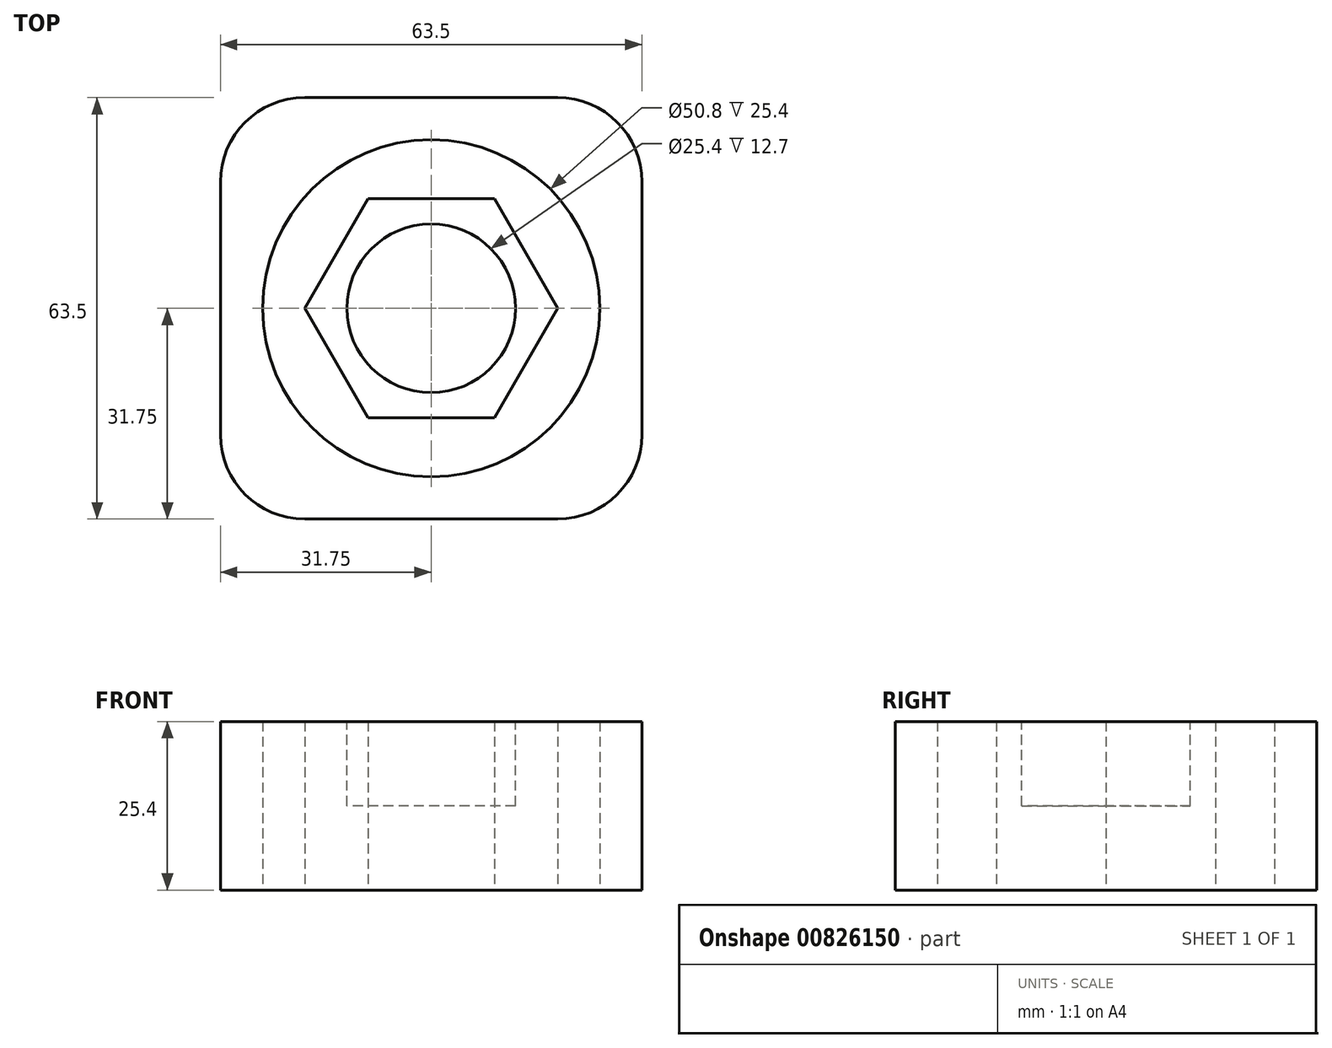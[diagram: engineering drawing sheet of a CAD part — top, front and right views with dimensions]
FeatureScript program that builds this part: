
annotation { "Feature Type Name" : "Feature", "Feature Type Description" : "" }
export const myFeature = defineFeature(function(context is Context, id is Id, definition is map)
    precondition{}
    {
        {
            var Q0;
            Q0=qCreatedBy(makeId("Top.planeOp"),FACE);
            var sketch = newSketch(context, id + "F0", { "sketchPlane" : qUnion([Q0])});
            skCircle(sketch, "E0", {"center": v(0, 0) * mm, "radius": 25.4 * mm});
            skLineSegment(sketch, "E1.bottom", {"start": v(19.05, 31.75) * mm, "end": v(-19.05, 31.75) * mm});
            skLineSegment(sketch, "E1.top", {"start": v(19.05, -31.75) * mm, "end": v(-19.05, -31.75) * mm});
            skLineSegment(sketch, "E1.left", {"start": v(31.75, 19.05) * mm, "end": v(31.75, -19.05) * mm});
            skLineSegment(sketch, "E1.right", {"start": v(-31.75, 19.05) * mm, "end": v(-31.75, -19.05) * mm});
            skCircle(sketch, "E2.cCircle", {"center": v(0, 0) * mm, "radius": 19.05 * mm, "construction": true});
            skLineSegment(sketch, "E2.0", {"start": v(9.53, -16.5) * mm, "end": v(-9.52, -16.5) * mm});
            skLineSegment(sketch, "E2.1", {"start": v(-9.52, -16.5) * mm, "end": v(-19.05, 0) * mm});
            skLineSegment(sketch, "E2.2", {"start": v(-19.05, 0) * mm, "end": v(-9.53, 16.5) * mm});
            skLineSegment(sketch, "E2.3", {"start": v(-9.53, 16.5) * mm, "end": v(9.52, 16.5) * mm});
            skLineSegment(sketch, "E2.4", {"start": v(9.52, 16.5) * mm, "end": v(19.05, 0) * mm});
            skLineSegment(sketch, "E2.5", {"start": v(19.05, 0) * mm, "end": v(9.52, -16.5) * mm});
            skPoint(sketch, "E3.visualSharp", {"position": v(-31.75, 31.75) * mm});
            skArc(sketch, "E3.filletArc", {"start": v(-19.05, 31.75) * mm, "mid": v(-28.03, 28.03) * mm, "end": v(-31.75, 19.05) * mm});
            skPoint(sketch, "E4.visualSharp", {"position": v(31.75, 31.75) * mm});
            skArc(sketch, "E4.filletArc", {"start": v(31.75, 19.05) * mm, "mid": v(28.03, 28.03) * mm, "end": v(19.05, 31.75) * mm});
            skPoint(sketch, "E5.visualSharp", {"position": v(31.75, -31.75) * mm});
            skArc(sketch, "E5.filletArc", {"start": v(19.05, -31.75) * mm, "mid": v(28.03, -28.03) * mm, "end": v(31.75, -19.05) * mm});
            skPoint(sketch, "E6.visualSharp", {"position": v(-31.75, -31.75) * mm});
            skArc(sketch, "E6.filletArc", {"start": v(-31.75, -19.05) * mm, "mid": v(-28.03, -28.03) * mm, "end": v(-19.05, -31.75) * mm});
            skSolve(sketch);
        }
        {
            var Q0;
            Q0=makeQuery(id+"F0.imprint","IMPRINT",FACE,{"disambiguationData":[TD([[makeQuery(id+"F0.imprint","IMPRINT",EDGE,{"derivedFrom":sQuery(id+"F0.wireOp",EDGE,"E0")}),-1.0]])]});
            var Q1;
            Q1=makeQuery(id+"F0.imprint","IMPRINT",FACE,{"disambiguationData":[TD([[makeQuery(id+"F0.imprint","IMPRINT",EDGE,{"derivedFrom":sQuery(id+"F0.wireOp",EDGE,"E2.0")}),-1.0]])]});
            extrude(context, id + "F1", {"entities" : qUnion([Q0, Q1]), "depth" : 25.4 * mm, "offsetDistance" : 25.4 * mm});
        }
        {
            var Q0;
            Q0=makeQuery(id+"F1.opExtrude","CAP_FACE",FACE,{"disambiguationData":[OSD([sQuery(id+"F0.wireOp",EDGE,"E2.0"),sQuery(id+"F0.wireOp",EDGE,"E2.1"),sQuery(id+"F0.wireOp",EDGE,"E2.2"),sQuery(id+"F0.wireOp",EDGE,"E2.3"),sQuery(id+"F0.wireOp",EDGE,"E2.4"),sQuery(id+"F0.wireOp",EDGE,"E2.5")])],"isStart":false});
            var sketch = newSketch(context, id + "F2", { "sketchPlane" : qUnion([Q0])});
            skCircle(sketch, "E7", {"center": v(0, 0) * mm, "radius": 12.7 * mm});
            skPoint(sketch, "E7.centerSnap0", {"position": v(0, 16.5) * mm});
            skSolve(sketch);
        }
        {
            var Q0;
            Q0 = qSketchRegion(id + "F2", true);
            extrude(context, id + "F3", {"entities" : qUnion([Q0]), "operationType" : NewBodyOperationType.REMOVE, "oppositeDirection" : true, "depth" : 12.7 * mm, "offsetDistance" : 25.4 * mm});
        }
    });
